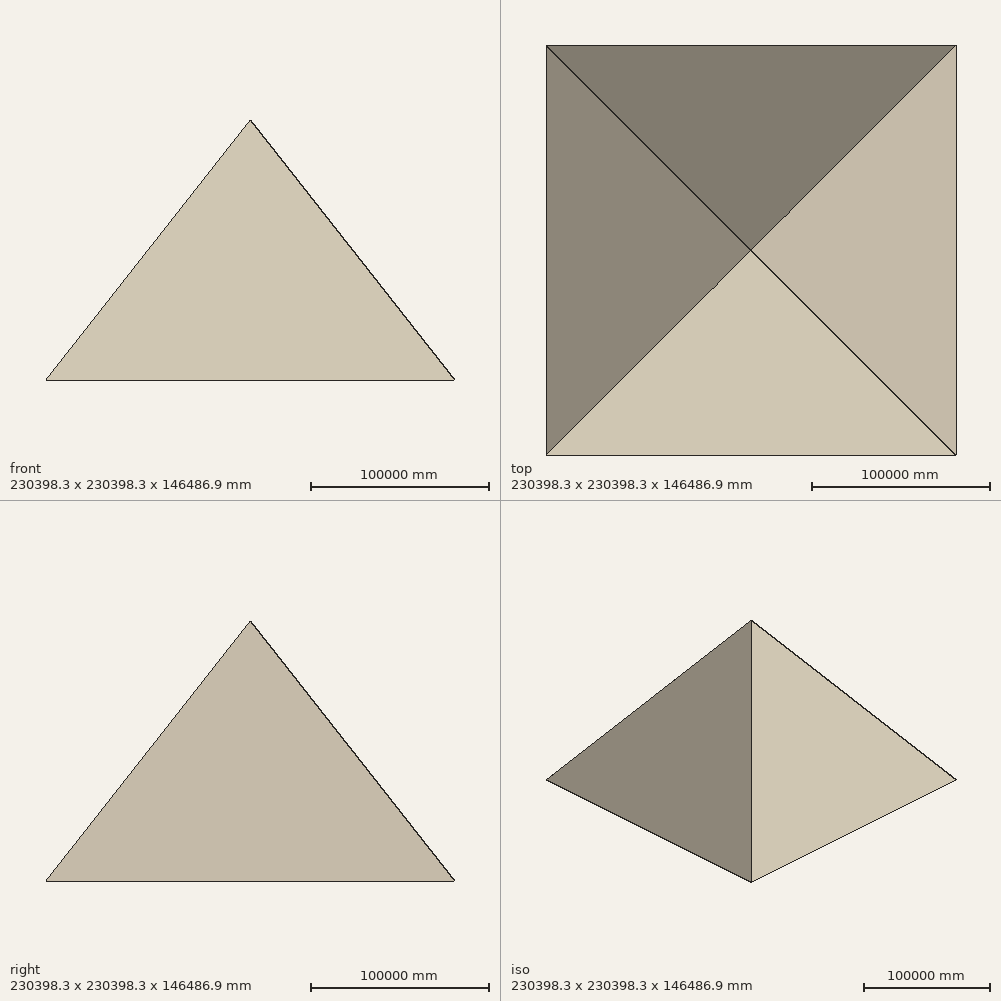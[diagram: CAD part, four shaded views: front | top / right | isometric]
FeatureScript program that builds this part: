
annotation { "Feature Type Name" : "Feature", "Feature Type Description" : "" }
export const myFeature = defineFeature(function(context is Context, id is Id, definition is map)
    precondition{}
    {
        {
            var Q0;
            Q0=qCreatedBy(makeId("Top.planeOp"),FACE);
            var sketch = newSketch(context, id + "F0", { "sketchPlane" : qUnion([Q0])});
            skLineSegment(sketch, "E0.rect.bottom", {"start": v(115199.16, 115199.16) * mm, "end": v(-115199.16, 115199.16) * mm});
            skLineSegment(sketch, "E0.rect.top", {"start": v(115199.16, -115199.16) * mm, "end": v(-115199.16, -115199.16) * mm});
            skLineSegment(sketch, "E0.rect.left", {"start": v(115199.16, 115199.16) * mm, "end": v(115199.16, -115199.16) * mm});
            skLineSegment(sketch, "E0.rect.right", {"start": v(-115199.16, 115199.16) * mm, "end": v(-115199.16, -115199.16) * mm});
            skPoint(sketch, "E0.rect.middle", {"position": v(0, 0) * mm});
            skSolve(sketch);
        }
        {
            var Q0;
            Q0 = qSketchRegion(id + "F0", true);
            extrude(context, id + "F1", {"entities" : qUnion([Q0]), "depth" : 146486.88 * mm});
        }
        {
            var Q0;
            Q0=makeQuery(id+"F1.opExtrude","CAP_FACE",FACE,{"disambiguationData":[OSD([sQuery(id+"F0.wireOp",EDGE,"E0.rect.bottom"),sQuery(id+"F0.wireOp",EDGE,"E0.rect.top"),sQuery(id+"F0.wireOp",EDGE,"E0.rect.left"),sQuery(id+"F0.wireOp",EDGE,"E0.rect.right")])],"isStart":false});
            chamfer(context, id + "F2", {"entities" : qUnion([Q0]), "chamferType" : ChamferType.TWO_OFFSETS, "width1" : 115199.16 * mm, "oppositeDirection" : false, "width2" : 146486.88 * mm, "tangentPropagation" : true});
        }
    });
